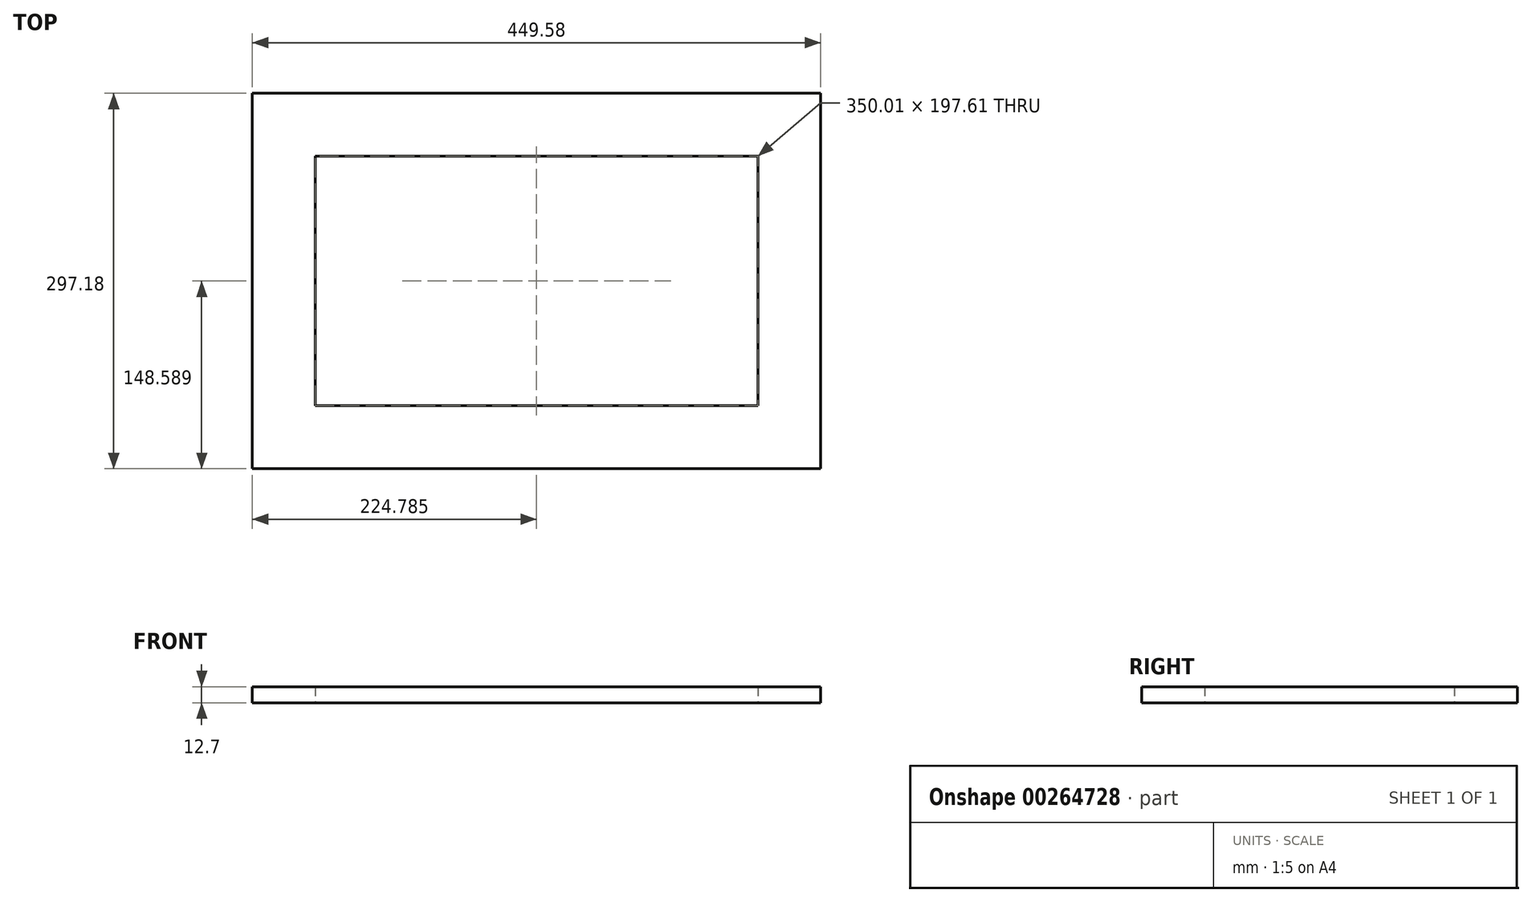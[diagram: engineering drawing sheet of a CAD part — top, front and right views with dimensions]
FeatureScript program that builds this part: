
annotation { "Feature Type Name" : "Feature", "Feature Type Description" : "" }
export const myFeature = defineFeature(function(context is Context, id is Id, definition is map)
    precondition{}
    {
        {
            var Q0;
            Q0=qCreatedBy(makeId("Top.planeOp"),FACE);
            var sketch = newSketch(context, id + "F0", { "sketchPlane" : qUnion([Q0])});
            skLineSegment(sketch, "E0.bottom", {"start": v(-301.02, 174.1) * mm, "end": v(148.56, 174.1) * mm});
            skLineSegment(sketch, "E0.top", {"start": v(-301.02, -123.07) * mm, "end": v(148.56, -123.07) * mm});
            skLineSegment(sketch, "E0.left", {"start": v(-301.02, 174.1) * mm, "end": v(-301.02, -123.07) * mm});
            skLineSegment(sketch, "E0.right", {"start": v(148.56, 174.1) * mm, "end": v(148.56, -123.07) * mm});
            skLineSegment(sketch, "E1.0", {"start": v(-251.24, 124.32) * mm, "end": v(98.77, 124.32) * mm});
            skLineSegment(sketch, "E1.1", {"start": v(-251.24, 124.32) * mm, "end": v(-251.24, -73.29) * mm});
            skLineSegment(sketch, "E1.2", {"start": v(-251.24, -73.29) * mm, "end": v(98.77, -73.29) * mm});
            skLineSegment(sketch, "E1.3", {"start": v(98.77, 124.32) * mm, "end": v(98.77, -73.29) * mm});
            skSolve(sketch);
        }
        {
            var Q0;
            Q0=makeQuery(id+"F0.imprint","IMPRINT",FACE,{"disambiguationData":[TD([[makeQuery(id+"F0.imprint","IMPRINT",EDGE,{"derivedFrom":sQuery(id+"F0.wireOp",EDGE,"E0.bottom")}),-1.0]])]});
            extrude(context, id + "F1", {"entities" : qUnion([Q0]), "depth" : 12.7 * mm});
        }
    });
